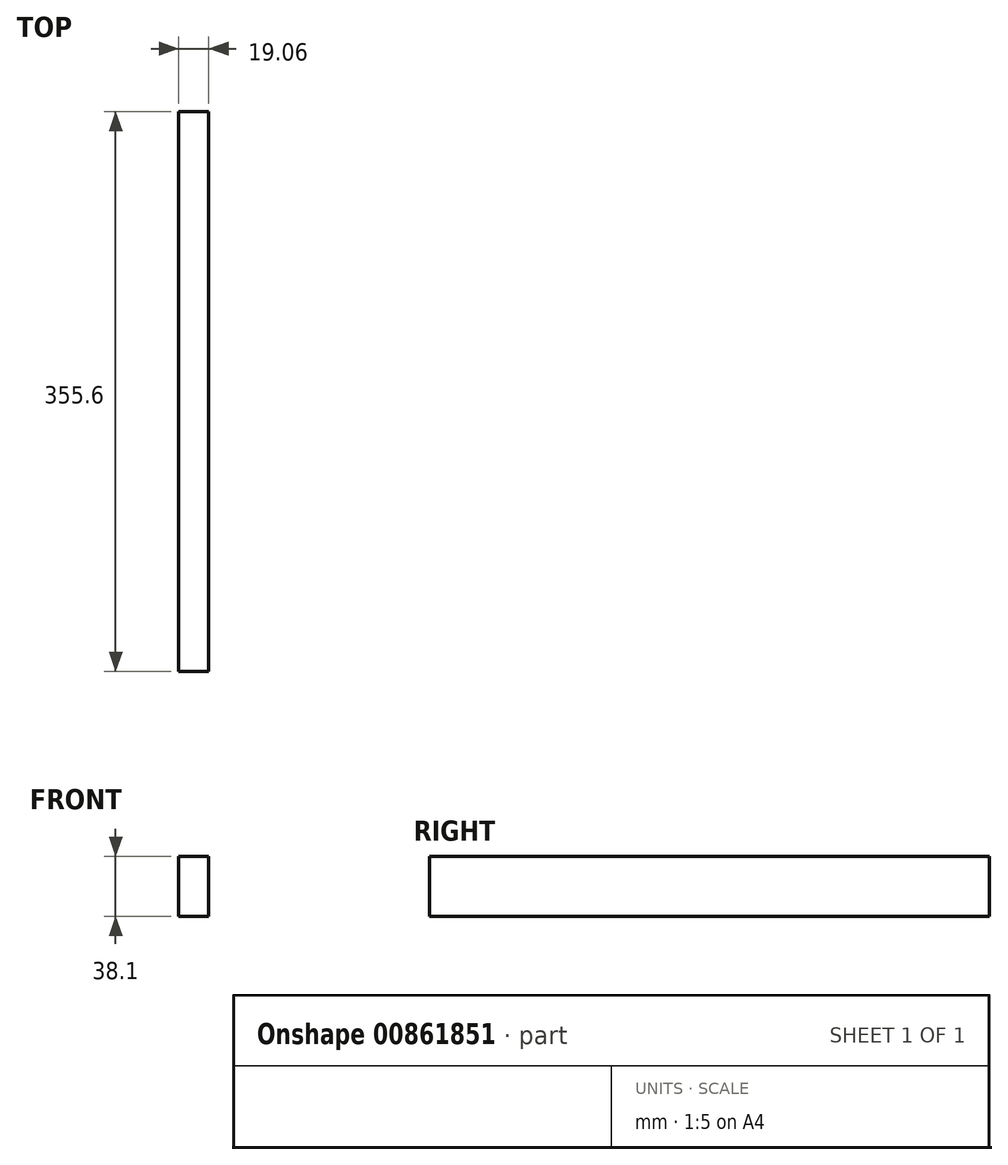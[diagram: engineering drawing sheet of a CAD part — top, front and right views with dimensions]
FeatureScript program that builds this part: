
annotation { "Feature Type Name" : "Feature", "Feature Type Description" : "" }
export const myFeature = defineFeature(function(context is Context, id is Id, definition is map)
    precondition{}
    {
        {
            var Q0;
            Q0=qCreatedBy(makeId("Front.planeOp"),FACE);
            var sketch = newSketch(context, id + "F0", { "sketchPlane" : qUnion([Q0])});
            skLineSegment(sketch, "E0.bottom", {"start": v(9.53, 19.05) * mm, "end": v(-9.53, 19.05) * mm});
            skLineSegment(sketch, "E0.top", {"start": v(9.53, -19.05) * mm, "end": v(-9.53, -19.05) * mm});
            skLineSegment(sketch, "E0.left", {"start": v(9.53, 19.05) * mm, "end": v(9.53, -19.05) * mm});
            skLineSegment(sketch, "E0.right", {"start": v(-9.52, 19.05) * mm, "end": v(-9.53, -19.05) * mm});
            skPoint(sketch, "E0.middle", {"position": v(0, 0) * mm});
            skSolve(sketch);
        }
        {
            var Q0;
            Q0=makeQuery(id+"F0.imprint","IMPRINT",FACE,{"disambiguationData":[TD([[makeQuery(id+"F0.imprint","IMPRINT",EDGE,{"derivedFrom":sQuery(id+"F0.wireOp",EDGE,"E0.bottom")}),1.0]])]});
            extrude(context, id + "F1", {"entities" : qUnion([Q0]), "depth" : 355.6 * mm, "offsetDistance" : 25.4 * mm});
        }
    });
